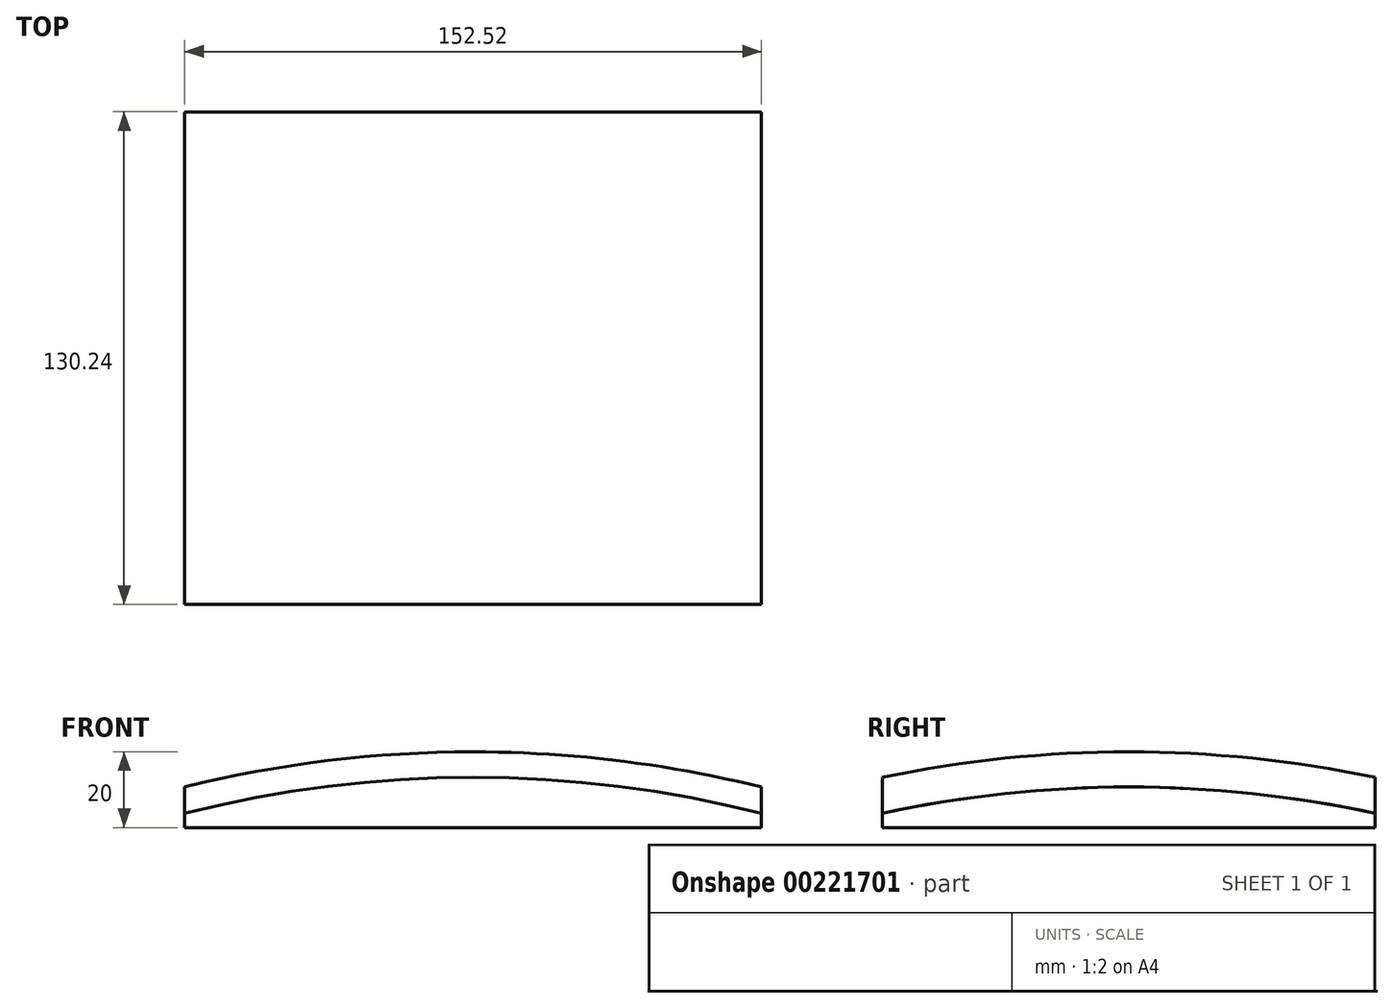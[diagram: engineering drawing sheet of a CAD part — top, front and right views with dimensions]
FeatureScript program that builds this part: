
annotation { "Feature Type Name" : "Feature", "Feature Type Description" : "" }
export const myFeature = defineFeature(function(context is Context, id is Id, definition is map)
    precondition{}
    {
        {
            var Q0;
            Q0=qCreatedBy(makeId("Front.planeOp"),FACE);
            var sketch = newSketch(context, id + "F0", { "sketchPlane" : qUnion([Q0])});
            skLineSegment(sketch, "E0", {"start": v(0, -40) * mm, "end": v(185.7, -40) * mm});
            skArc(sketch, "E1", {"start": v(185.7, -40) * mm, "mid": v(97.58, 4.63) * mm, "end": v(0, 20) * mm});
            skPoint(sketch, "E2.orphan", {"position": v(-185.7, -40) * mm});
            skLineSegment(sketch, "E3", {"start": v(0, -40) * mm, "end": v(0, 20) * mm});
            skSolve(sketch);
        }
        {
            var Q0;
            Q0 = qSketchRegion(id + "F0", true);
            var Q1;
            Q1=sQuery(id+"F0.wireOp",EDGE,"E3");
            revolve(context, id + "F1", {"entities" : qUnion([Q0]), "axis" : qUnion([Q1]), "revolveType" : RevolveType.FULL});
        }
        {
            var Q0;
            Q0=qCreatedBy(makeId("Top.planeOp"),FACE);
            var sketch = newSketch(context, id + "F2", { "sketchPlane" : qUnion([Q0])});
            skLineSegment(sketch, "E4.bottom", {"start": v(76.26, -65.12) * mm, "end": v(-76.26, -65.12) * mm});
            skLineSegment(sketch, "E4.top", {"start": v(76.26, 65.12) * mm, "end": v(-76.26, 65.12) * mm});
            skLineSegment(sketch, "E4.left", {"start": v(76.26, -65.12) * mm, "end": v(76.26, 65.12) * mm});
            skLineSegment(sketch, "E4.right", {"start": v(-76.26, -65.12) * mm, "end": v(-76.26, 65.12) * mm});
            skPoint(sketch, "E4.middle", {"position": v(0, 0) * mm});
            skSolve(sketch);
        }
        {
            var Q0;
            Q0 = qSketchRegion(id + "F2", true);
            extrude(context, id + "F3", {"entities" : qUnion([Q0]), "depth" : 36.1 * mm});
        }
        {
            var Q0;
            Q0=makeQuery(id+"F1.opRevolve","SWEPT_BODY",BODY,{"disambiguationData":[OSD([sQuery(id+"F0.wireOp",EDGE,"E0"),sQuery(id+"F0.wireOp",EDGE,"E1"),sQuery(id+"F0.wireOp",EDGE,"E3")])]});
            var Q1;
            Q1=makeQuery(id+"F3.opExtrude","SWEPT_BODY",BODY,{"disambiguationData":[OSD([sQuery(id+"F2.wireOp",EDGE,"E4.bottom"),sQuery(id+"F2.wireOp",EDGE,"E4.top"),sQuery(id+"F2.wireOp",EDGE,"E4.left"),sQuery(id+"F2.wireOp",EDGE,"E4.right")])]});
            booleanBodies(context, id + "F4", {"operationType" : BooleanOperationType.INTERSECTION, "tools" : qUnion([Q0, Q1])});
        }
    });
